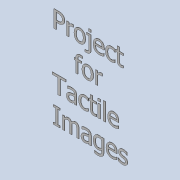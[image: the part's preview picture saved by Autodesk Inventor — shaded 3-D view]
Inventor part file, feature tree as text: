
AUTODESK INVENTOR PART (.ipt)
format: ipt  version: 2020 (Build 240168000, 168)  size: 668,672 bytes
history: native  units: mm
features: extrude x1, sketch x1
ambient origin geometry x8: Origin, YZ Plane, XZ Plane, XY Plane, X Axis, Y Axis, Z Axis, Center Point
bodies: Solid1 (feature_tree)
feature tree (2):
  extrude  "Extrusion1"  Depth=200.0mm
  sketch  "Sketch1"  dims[d0=300.0mm d1=200.0mm d2=0.6mm d3=0.0mm d4=50.0mm d5=50.0mm d6=20.0mm]
